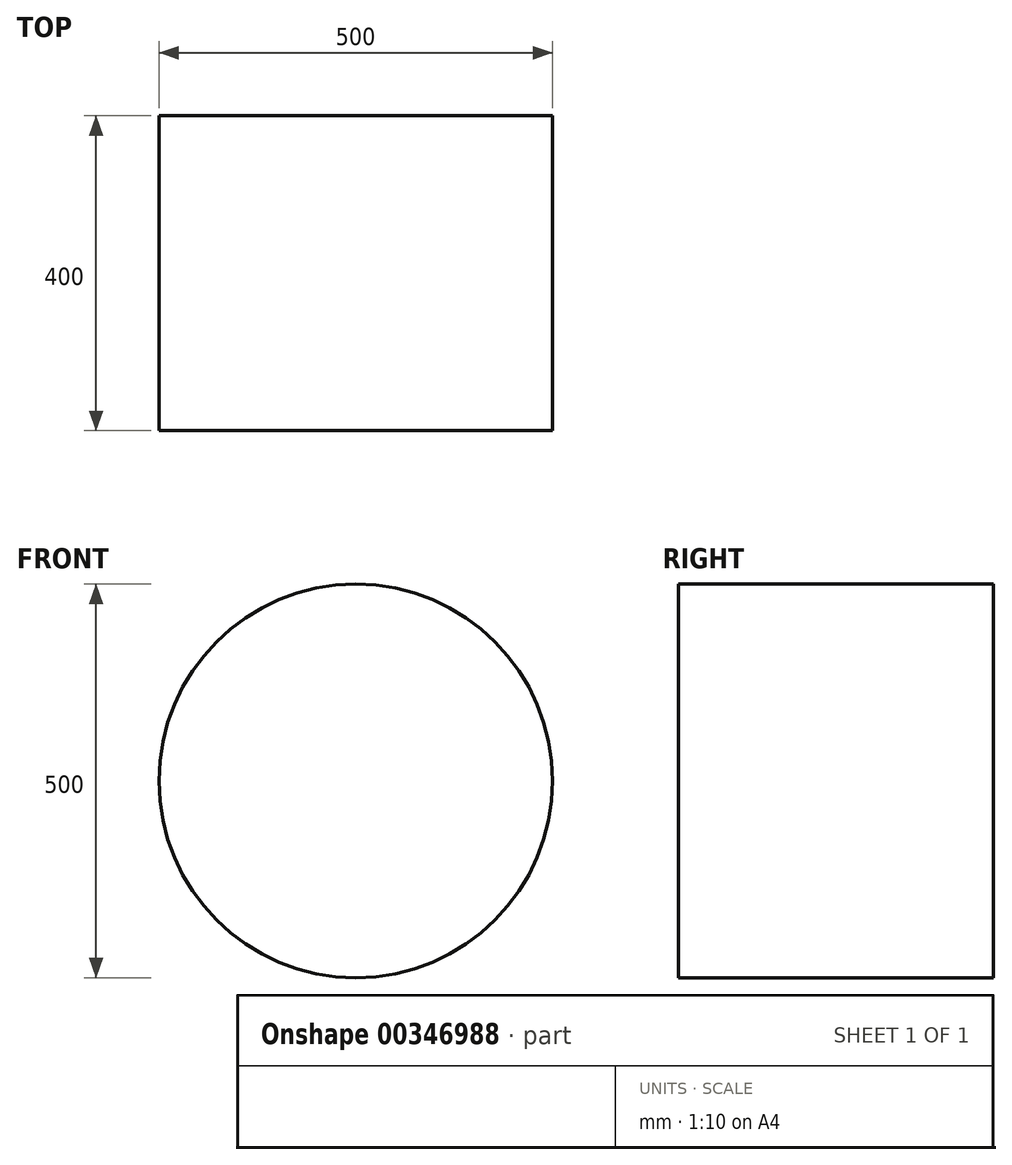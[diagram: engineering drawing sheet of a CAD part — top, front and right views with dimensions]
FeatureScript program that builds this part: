
annotation { "Feature Type Name" : "Feature", "Feature Type Description" : "" }
export const myFeature = defineFeature(function(context is Context, id is Id, definition is map)
    precondition{}
    {
        {
            var Q0;
            Q0=qCreatedBy(makeId("Front.planeOp"),FACE);
            var sketch = newSketch(context, id + "F0", { "sketchPlane" : qUnion([Q0])});
            skCircle(sketch, "E0", {"center": v(0, 0) * mm, "radius": 250 * mm});
            skSolve(sketch);
        }
        {
            var Q0;
            Q0 = qSketchRegion(id + "F0", true);
            extrude(context, id + "F1", {"entities" : qUnion([Q0]), "endBound" : BoundingType.SYMMETRIC, "depth" : 400 * mm});
        }
    });
